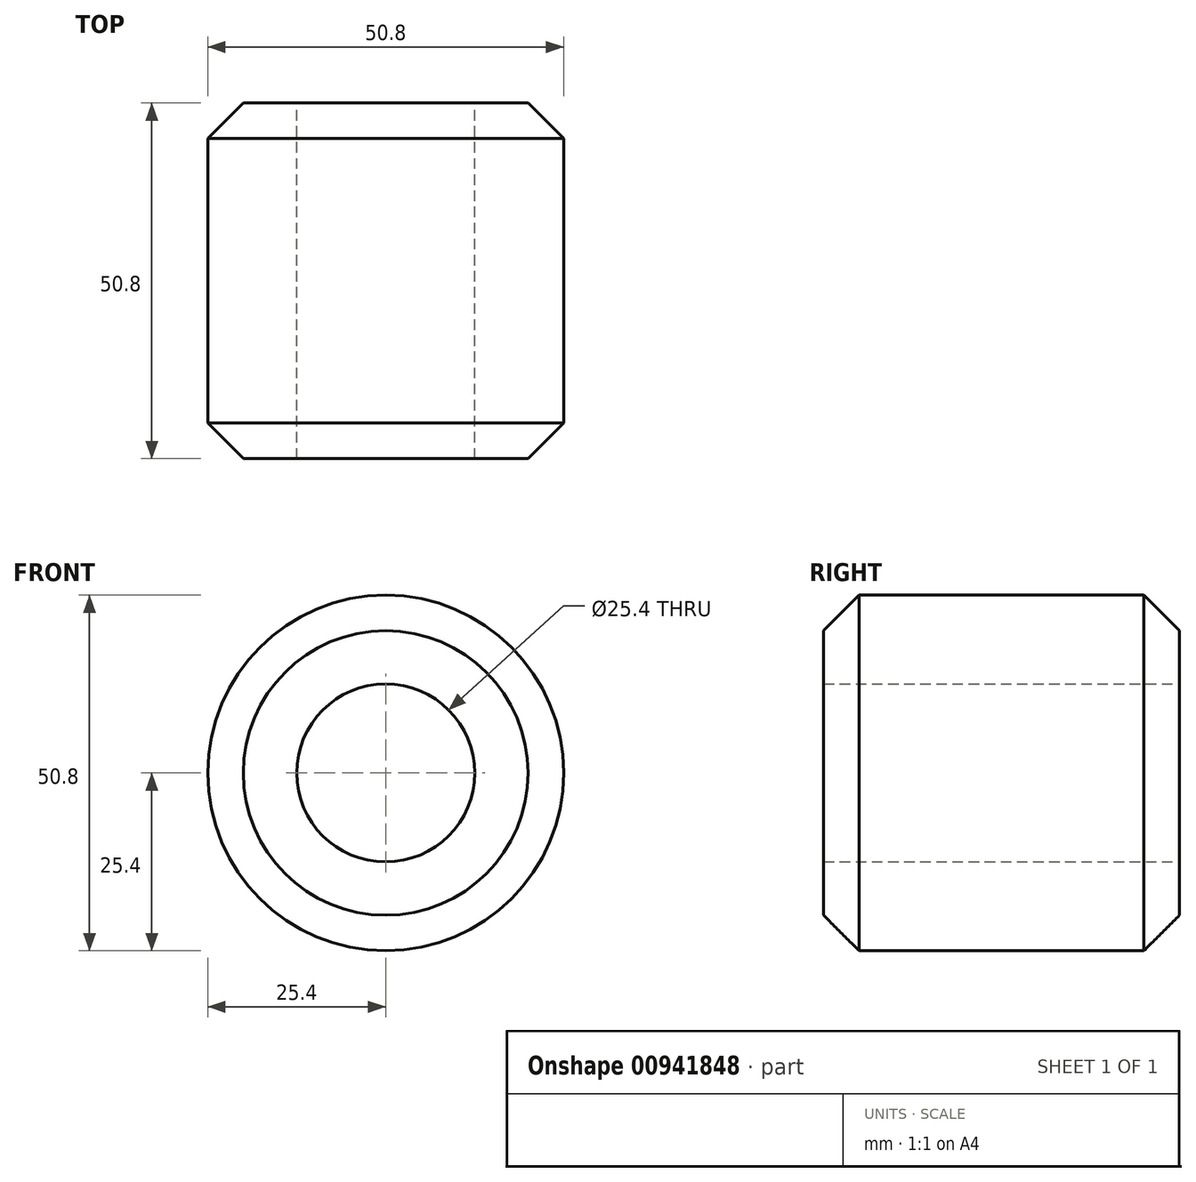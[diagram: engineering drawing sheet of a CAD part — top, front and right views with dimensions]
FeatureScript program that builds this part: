
annotation { "Feature Type Name" : "Feature", "Feature Type Description" : "" }
export const myFeature = defineFeature(function(context is Context, id is Id, definition is map)
    precondition{}
    {
        {
            var Q0;
            Q0=qCreatedBy(makeId("Front.planeOp"),FACE);
            var sketch = newSketch(context, id + "F0", { "sketchPlane" : qUnion([Q0])});
            skCircle(sketch, "E0", {"center": v(0, 0) * mm, "radius": 25.4 * mm});
            skSolve(sketch);
        }
        {
            var Q0;
            Q0 = qSketchRegion(id + "F0", true);
            extrude(context, id + "F1", {"entities" : qUnion([Q0]), "depth" : 50.8 * mm, "offsetDistance" : 25.4 * mm});
        }
        {
            var Q0;
            Q0=makeQuery(id+"F1.opExtrude","CAP_EDGE",EDGE,{"disambiguationData":[OSD([sQuery(id+"F0.wireOp",EDGE,"E0")])],"isStart":false});
            chamfer(context, id + "F2", {"entities" : qUnion([Q0]), "width" : 5.08 * mm, "tangentPropagation" : true});
        }
        {
            var Q0;
            Q0=makeQuery(id+"F1.opExtrude","CAP_EDGE",EDGE,{"disambiguationData":[OSD([sQuery(id+"F0.wireOp",EDGE,"E0")])],"isStart":true});
            chamfer(context, id + "F3", {"entities" : qUnion([Q0]), "width" : 5.08 * mm, "tangentPropagation" : true});
        }
        {
            var Q0;
            Q0=qCreatedBy(makeId("Front.planeOp"),FACE);
            var sketch = newSketch(context, id + "F4", { "sketchPlane" : qUnion([Q0])});
            skCircle(sketch, "E1", {"center": v(0, 0) * mm, "radius": 12.7 * mm});
            skSolve(sketch);
        }
        {
            var Q0;
            Q0 = qSketchRegion(id + "F4", true);
            extrude(context, id + "F5", {"entities" : qUnion([Q0]), "operationType" : NewBodyOperationType.REMOVE, "depth" : 50.8 * mm, "offsetDistance" : 25.4 * mm});
        }
    });
